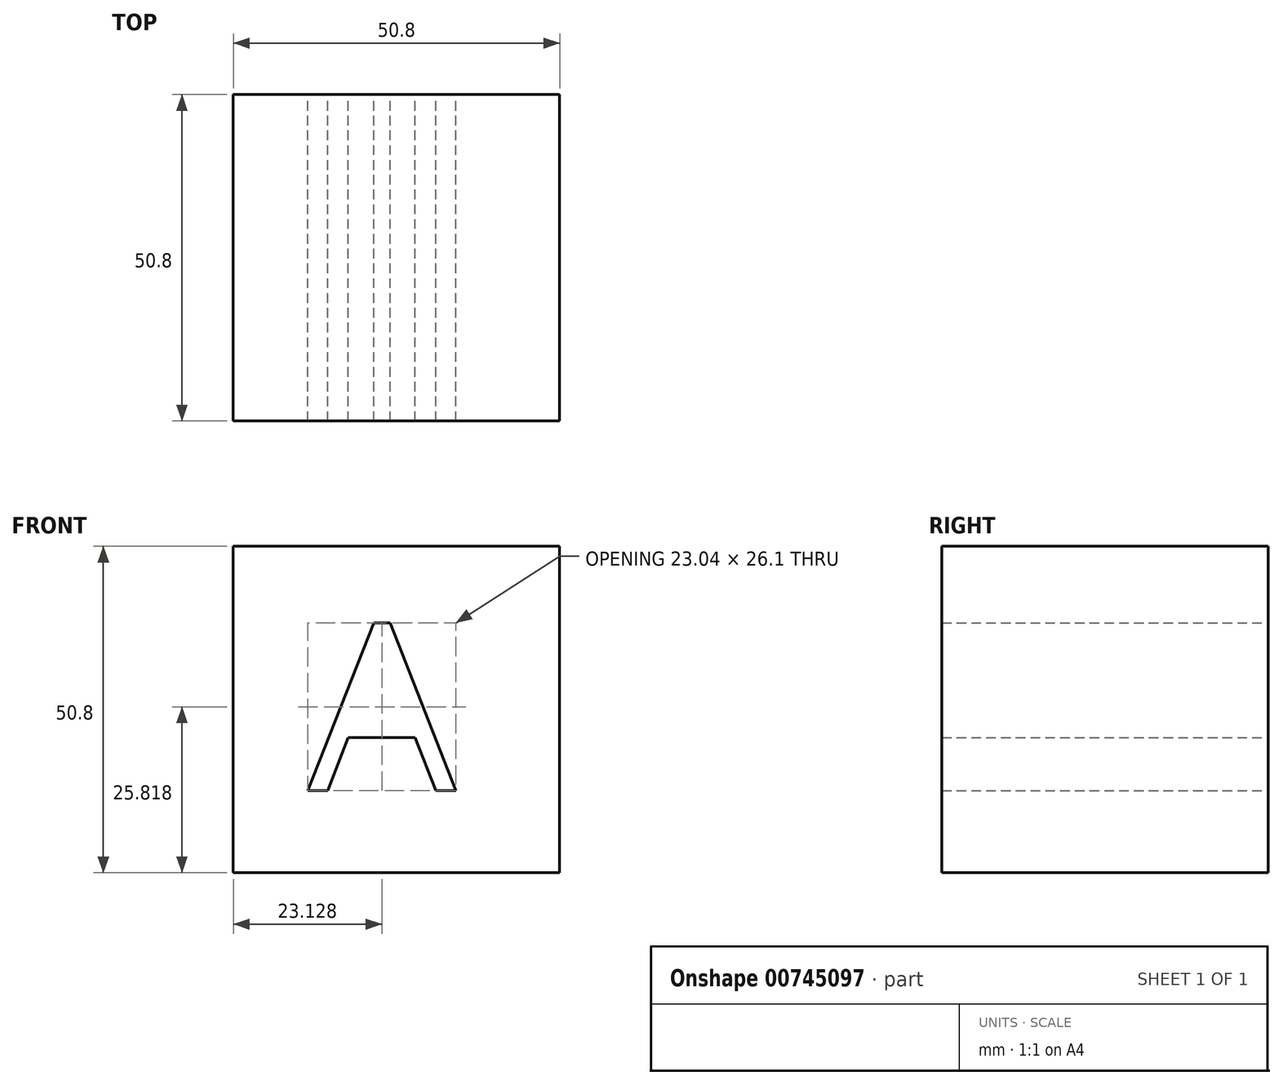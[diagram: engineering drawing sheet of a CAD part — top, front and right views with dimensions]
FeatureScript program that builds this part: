
annotation { "Feature Type Name" : "Feature", "Feature Type Description" : "" }
export const myFeature = defineFeature(function(context is Context, id is Id, definition is map)
    precondition{}
    {
        {
            var Q0;
            Q0=qCreatedBy(makeId("Front.planeOp"),FACE);
            var sketch = newSketch(context, id + "F0", { "sketchPlane" : qUnion([Q0])});
            skLineSegment(sketch, "E0.bottom", {"start": v(27.9, 25.4) * mm, "end": v(-22.9, 25.4) * mm});
            skLineSegment(sketch, "E0.top", {"start": v(27.9, -25.4) * mm, "end": v(-22.9, -25.4) * mm});
            skLineSegment(sketch, "E0.left", {"start": v(27.9, 25.4) * mm, "end": v(27.9, -25.4) * mm});
            skLineSegment(sketch, "E0.right", {"start": v(-22.9, 25.4) * mm, "end": v(-22.9, -25.4) * mm});
            skPoint(sketch, "E0.middle", {"position": v(2.5, 0) * mm});
            skText(sketch, "E1", { "text": "A\n", "fontName": "OpenSans-Regular.ttf"});
            const initialGuessF0  = {"E1": [-0.01128, -0.01263, 1, 0, 0.02621]};
            skSetInitialGuess(sketch, initialGuessF0);
            skSolve(sketch);
        }
        {
            var Q0;
            Q0 = qSketchRegion(id + "F0", true);
            extrude(context, id + "F1", {"entities" : qUnion([Q0]), "endBound" : BoundingType.SYMMETRIC, "depth" : 50.8 * mm, "offsetDistance" : 25.4 * mm});
        }
    });
